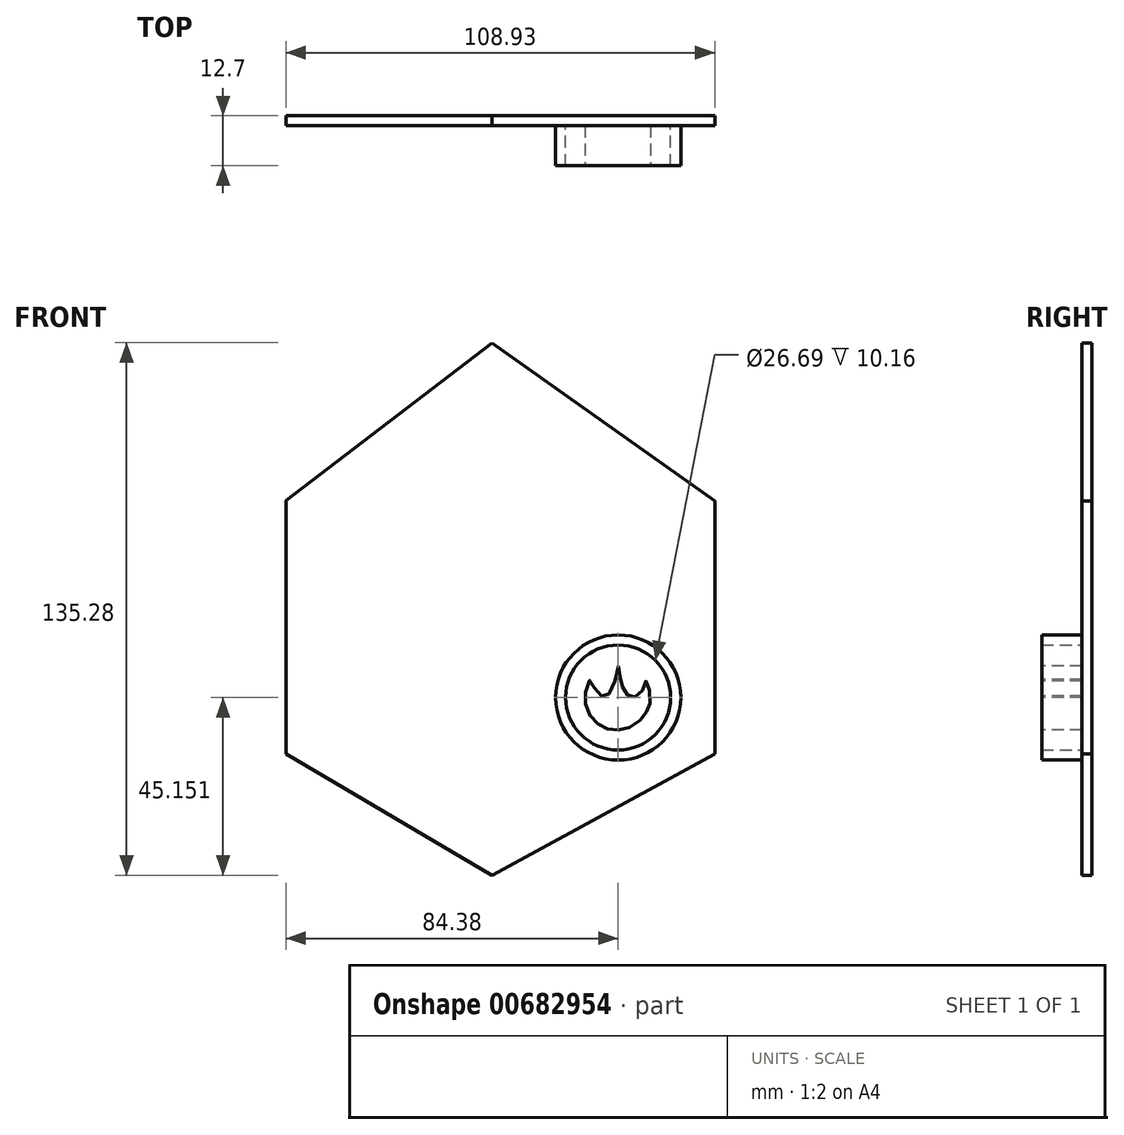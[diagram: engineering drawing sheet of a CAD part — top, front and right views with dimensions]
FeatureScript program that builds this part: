
annotation { "Feature Type Name" : "Feature", "Feature Type Description" : "" }
export const myFeature = defineFeature(function(context is Context, id is Id, definition is map)
    precondition{}
    {
        {
            var Q0;
            Q0=qCreatedBy(makeId("Front.planeOp"),FACE);
            var sketch = newSketch(context, id + "F0", { "sketchPlane" : qUnion([Q0])});
            skLineSegment(sketch, "E0", {"start": v(0, 68.56) * mm, "end": v(59.23, 26.56) * mm});
            skLineSegment(sketch, "E1", {"start": v(59.23, 26.56) * mm, "end": v(59.23, -40.56) * mm});
            skLineSegment(sketch, "E2", {"start": v(59.23, -40.56) * mm, "end": v(0, -72.79) * mm});
            skLineSegment(sketch, "E3", {"start": v(0, -72.79) * mm, "end": v(-54.78, -40.56) * mm});
            skLineSegment(sketch, "E4", {"start": v(-54.78, -40.56) * mm, "end": v(-54.78, 26.56) * mm});
            skLineSegment(sketch, "E5", {"start": v(-54.78, 26.56) * mm, "end": v(0, 68.56) * mm});
            skSolve(sketch);
        }
        {
            var Q0;
            Q0=makeQuery(id+"F0.imprint","IMPRINT",FACE,{"disambiguationData":[TD([[makeQuery(id+"F0.imprint","IMPRINT",EDGE,{"derivedFrom":sQuery(id+"F0.wireOp",EDGE,"E0")}),-1.0]])]});
            extrude(context, id + "F1", {"entities" : qUnion([Q0]), "depth" : 12.7 * mm, "offsetDistance" : 25.4 * mm});
        }
        {
            var Q0;
            Q0=makeQuery(id+"F1.opExtrude","CAP_FACE",FACE,{"disambiguationData":[OSD([sQuery(id+"F0.wireOp",EDGE,"E0"),sQuery(id+"F0.wireOp",EDGE,"E1"),sQuery(id+"F0.wireOp",EDGE,"E2"),sQuery(id+"F0.wireOp",EDGE,"E3"),sQuery(id+"F0.wireOp",EDGE,"E4"),sQuery(id+"F0.wireOp",EDGE,"E5")])],"isStart":false});
            extrude(context, id + "F2", {"entities" : qUnion([Q0]), "operationType" : NewBodyOperationType.REMOVE, "oppositeDirection" : true, "depth" : 2.54 * mm, "offsetDistance" : 25.4 * mm});
        }
        {
            var Q0;
            Q0=makeQuery(id+"F2.boolean.opBoolean","COPY",FACE,{"derivedFrom":makeQuery(id+"F2.opExtrude","CAP_FACE",FACE,{"disambiguationData":[OSD([sQuery(id+"F0.wireOp",EDGE,"E0"),sQuery(id+"F0.wireOp",EDGE,"E1"),sQuery(id+"F0.wireOp",EDGE,"E2"),sQuery(id+"F0.wireOp",EDGE,"E3"),sQuery(id+"F0.wireOp",EDGE,"E4"),sQuery(id+"F0.wireOp",EDGE,"E5")])],"isStart":false})});
            extrude(context, id + "F3", {"entities" : qUnion([Q0]), "operationType" : NewBodyOperationType.REMOVE, "oppositeDirection" : true, "depth" : 7.62 * mm, "offsetDistance" : 25.4 * mm});
        }
        {
            var Q0;
            Q0=makeQuery(id+"F1.opExtrude","SWEPT_FACE",FACE,{"disambiguationData":[OSD([sQuery(id+"F0.wireOp",EDGE,"E0")])]});
            extrude(context, id + "F4", {"entities" : qUnion([Q0]), "operationType" : NewBodyOperationType.REMOVE, "oppositeDirection" : true, "depth" : 2.54 * mm, "offsetDistance" : 25.4 * mm});
        }
        {
            var Q0;
            Q0=makeQuery(id+"F1.opExtrude","SWEPT_FACE",FACE,{"disambiguationData":[OSD([sQuery(id+"F0.wireOp",EDGE,"E5")])]});
            extrude(context, id + "F5", {"entities" : qUnion([Q0]), "operationType" : NewBodyOperationType.REMOVE, "oppositeDirection" : true, "depth" : 2.54 * mm, "offsetDistance" : 25.4 * mm});
        }
        {
            var Q0;
            Q0=makeQuery(id+"F1.opExtrude","SWEPT_FACE",FACE,{"disambiguationData":[OSD([sQuery(id+"F0.wireOp",EDGE,"E1")])]});
            extrude(context, id + "F6", {"entities" : qUnion([Q0]), "operationType" : NewBodyOperationType.REMOVE, "oppositeDirection" : true, "depth" : 2.54 * mm, "offsetDistance" : 25.4 * mm});
        }
        {
            var Q0;
            Q0=makeQuery(id+"F1.opExtrude","SWEPT_FACE",FACE,{"disambiguationData":[OSD([sQuery(id+"F0.wireOp",EDGE,"E4")])]});
            extrude(context, id + "F7", {"entities" : qUnion([Q0]), "operationType" : NewBodyOperationType.REMOVE, "oppositeDirection" : true, "depth" : 2.54 * mm, "offsetDistance" : 25.4 * mm});
        }
        {
            var Q0;
            Q0=makeQuery(id+"F1.opExtrude","SWEPT_FACE",FACE,{"disambiguationData":[OSD([sQuery(id+"F0.wireOp",EDGE,"E3")])]});
            extrude(context, id + "F8", {"entities" : qUnion([Q0]), "operationType" : NewBodyOperationType.REMOVE, "oppositeDirection" : true, "depth" : 2.54 * mm, "offsetDistance" : 25.4 * mm});
        }
        {
            var Q0;
            Q0=makeQuery(id+"F1.opExtrude","SWEPT_FACE",FACE,{"disambiguationData":[OSD([sQuery(id+"F0.wireOp",EDGE,"E2")])]});
            extrude(context, id + "F9", {"entities" : qUnion([Q0]), "operationType" : NewBodyOperationType.REMOVE, "oppositeDirection" : true, "depth" : 2.54 * mm, "offsetDistance" : 25.4 * mm});
        }
        {
            var Q0;
            Q0=makeQuery(id+"F3.boolean.opBoolean","COPY",FACE,{"derivedFrom":makeQuery(id+"F3.opExtrude","CAP_FACE",FACE,{"disambiguationData":[OSD([sQuery(id+"F0.wireOp",EDGE,"E0"),sQuery(id+"F0.wireOp",EDGE,"E1"),sQuery(id+"F0.wireOp",EDGE,"E2"),sQuery(id+"F0.wireOp",EDGE,"E3"),sQuery(id+"F0.wireOp",EDGE,"E4"),sQuery(id+"F0.wireOp",EDGE,"E5")])],"isStart":false})});
            var sketch = newSketch(context, id + "F10", { "sketchPlane" : qUnion([Q0])});
            skCircle(sketch, "E6", {"center": v(32.14, -24.72) * mm, "radius": 15.9 * mm});
            skCircle(sketch, "E7", {"center": v(32.14, -24.72) * mm, "radius": 13.34 * mm});
            skFitSpline(sketch, "E8", {"points": [v(32.25, -16.72) * mm, v(30.9, -22.27) * mm, v(29.47, -24.05) * mm, v(28.12, -24.33) * mm, v(26.64, -23.67) * mm, v(25.3, -20.12) * mm, v(24.22, -22.02) * mm, v(23.7, -25.1) * mm, v(24.22, -27.8) * mm, v(25.97, -30.64) * mm, v(27.92, -32.02) * mm, v(30.17, -32.84) * mm, v(32.78, -32.88) * mm, v(35.33, -32.15) * mm, v(38.01, -30.22) * mm, v(39.4, -28.29) * mm, v(40.15, -26.61) * mm, v(40.31, -24.06) * mm, v(39.33, -20.46) * mm, v(38.8, -21.64) * mm, v(37.85, -23.57) * mm, v(36.24, -24.62) * mm, v(34.97, -24.41) * mm, v(33.83, -23.12) * mm, v(33.06, -21.4) * mm, v(32.56, -18.62) * mm, v(32.25, -16.72) * mm]});
            skSolve(sketch);
        }
        {
            var Q0;
            Q0=makeQuery(id+"F10.imprint","IMPRINT",FACE,{"disambiguationData":[TD([[makeQuery(id+"F10.imprint","IMPRINT",EDGE,{"derivedFrom":sQuery(id+"F10.wireOp",EDGE,"E8")}),1.0]])]});
            var Q1;
            Q1=makeQuery(id+"F10.imprint","IMPRINT",FACE,{"disambiguationData":[TD([[makeQuery(id+"F10.imprint","IMPRINT",EDGE,{"derivedFrom":sQuery(id+"F10.wireOp",EDGE,"E6")}),1.0]])]});
            extrude(context, id + "F11", {"entities" : qUnion([Q0, Q1]), "operationType" : NewBodyOperationType.ADD, "depth" : 5.08 * mm, "offsetDistance" : 25.4 * mm});
        }
        {
            var Q0;
            Q0=makeQuery(id+"F11.opExtrude","CAP_FACE",FACE,{"disambiguationData":[OSD([sQuery(id+"F10.wireOp",EDGE,"E8")])],"isStart":false});
            var Q1;
            Q1=makeQuery(id+"F11.opExtrude","CAP_FACE",FACE,{"disambiguationData":[OSD([sQuery(id+"F10.wireOp",EDGE,"E6"),sQuery(id+"F10.wireOp",EDGE,"E7")])],"isStart":false});
            extrude(context, id + "F12", {"entities" : qUnion([Q0, Q1]), "operationType" : NewBodyOperationType.ADD, "depth" : 5.08 * mm, "offsetDistance" : 25.4 * mm});
        }
    });
